# Revit family: Soap_Dispenser-Bradley_Corp-Deck_Mounted-Metro-6-3300
name_source: partatom
category: Specialty Equipment
revit_build: Autodesk Revit 2018 (Build: 20170223_1515(x64)
units: mm (PartAtom-declared; Revit-internal decimal feet)

## family parameters
Cut with Voids When Loaded = No
Host = Face
Part Type = Normal
Room Calculation Point = No
Round Connector Dimension = Use Diameter
Shared = No

## types (1)
- Soap_Dispenser-Bradley_Corp-Deck_Mounted-Metro-6-3300
    Default Elevation = 48"
    Description = Touchless Deck Mounted Soap Dispenser -Verge Metro Series 6-3300, Paired with Metro Series S53-3300 Faucet
    Manufacturer Installation URL - English = https://www.bradleycorp.com
    Model = Verge Metro Series 6-33000
    Product Name = Verge Soap Dispenser - Metro Metro Series
    Product Page URL = https://www.bradleycorp.com
    Product Tech Data URL - English = https://www.bradleycorp.com
    Specifications URL = https://www.bradleycorp.com
    Type Comments = Touchless Deck Mounted Soap Dispenser -Verge Metro Series 6-3300, Paired with Metro Series S53-3300 Faucet

## geometry (parser evidence)
native form markers: Sweep x1
no freeform markers — native parametric forms only
